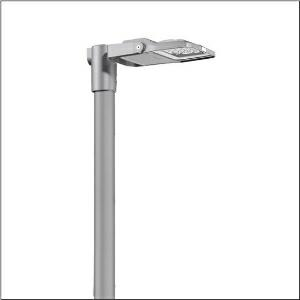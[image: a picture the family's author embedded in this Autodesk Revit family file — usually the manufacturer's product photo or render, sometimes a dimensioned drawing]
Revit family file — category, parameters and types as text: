
# Revit family: floodlight_fl_21_micro___pl64_5xa7762a4e3a_ee73
name_source: partatom
category: Lighting Fixtures
units: mm (PartAtom-declared; Revit-internal decimal feet)

## family parameters
Cut with Voids When Loaded = No
Host = Face
Light Source = No
Part Type = Normal
Room Calculation Point = No
Round Connector Dimension = Use Diameter
Shared = No

## types (1)
- --- (1 x LED, 2980 lm, 23.1 W, 4000K)
    Apparent Load = 23 VA
    CIE Flux Codes = 28 80 98 100 100
    Color Rendering = 70
    Color Temperature = 4000K
    Default Elevation = 1800 mm
    Description = Floodlight FL 21 micro, floodlight, primary light control with lens, of PMMA, primary optical cover: protective disc, of toughened safety glass, transparent, light distribution: PL64, light emission: direct distribution, installation type: surface-mounted, LED, High Power LED, rated luminous flux: 2.980lm, luminous efficacy: 129lm/W, light colour: 740, colour temperature: 4000K, control gear: ECG iQ, control: Auto-Match, Temp-Guard, Night-Set, Smart-Wire, Desk-Remote (wireless, voltage-free reading and setting of iQ features in the workshop via application-optimized NFC function/RFID function), optimised constant luminous flux control (CLO 2.0), Street-Remote, with terminal, 6-pole, mains connection: 220..240V, AC, 50/60Hz, start of lifetime: 23W, end of lifetime: 24W, reduction: 11W, luminaire housing, of diecast aluminium, powder-coated, Siteco® metallic grey (DB 702S), corrosivity category C5 according to DIN EN ISO 12944, mast bracket, of steel, galvanised, powder-coated, Siteco® metallic grey (DB 702S), protection rating (complete): IP66, insulation class (complete): insulation class II (safety insulation), certification: CE, protection symbol: D, impact resistance: IK07, permissible operating ambient temperature: -40..+40°C, permissible operating ambient temperature for outdoor applications: -40..+50°C, standard: DIN EN 12944, packaging unit: 1 piece

Light Distribution: PL64
    Height = 65 mm
    Lamp = 1 x LED
    Lamp Light Flux = 2980 lm
    Lamp Power = 23.1 W
    Lamp count = 1
    Length = 312 mm
    Luminous efficacy = 129 lm/W
    Manufacturer = Siteco
    ModVariant = No
    Model = 5XA7762A4E3A
    Number of Poles = 1
    OnlyDefault = Yes
    Power Factor = 1
    Product Name = Floodlight FL 21 micro | PL64
    Product group = floodlight | pylon top
    ProductGroupID = 6101
    Protection Class = Protection class II
    Protection Degree = IP 66
    RLX_Detail_Level = 1
    RlxData = <blob elided: 101441 chars, md5=61bfd7f8>
    Socket = socket
    Standby Power = 0 W
    System Light Flux = 2980 lm
    System Power = 23 W
    Type Comments = factory setting: luminous flux: 100 % | dim-lin: 254 | 455 mA
    Type Image = l_1007121.jpg
    URL = http://relux.com
    VarID = @adj_094059
    Voltage = 0 V
    Weight = 0.00 kg
    Width = 230 mm

## geometry (parser evidence)
native form markers: Blend x4, Sweep x11
no freeform markers — native parametric forms only
